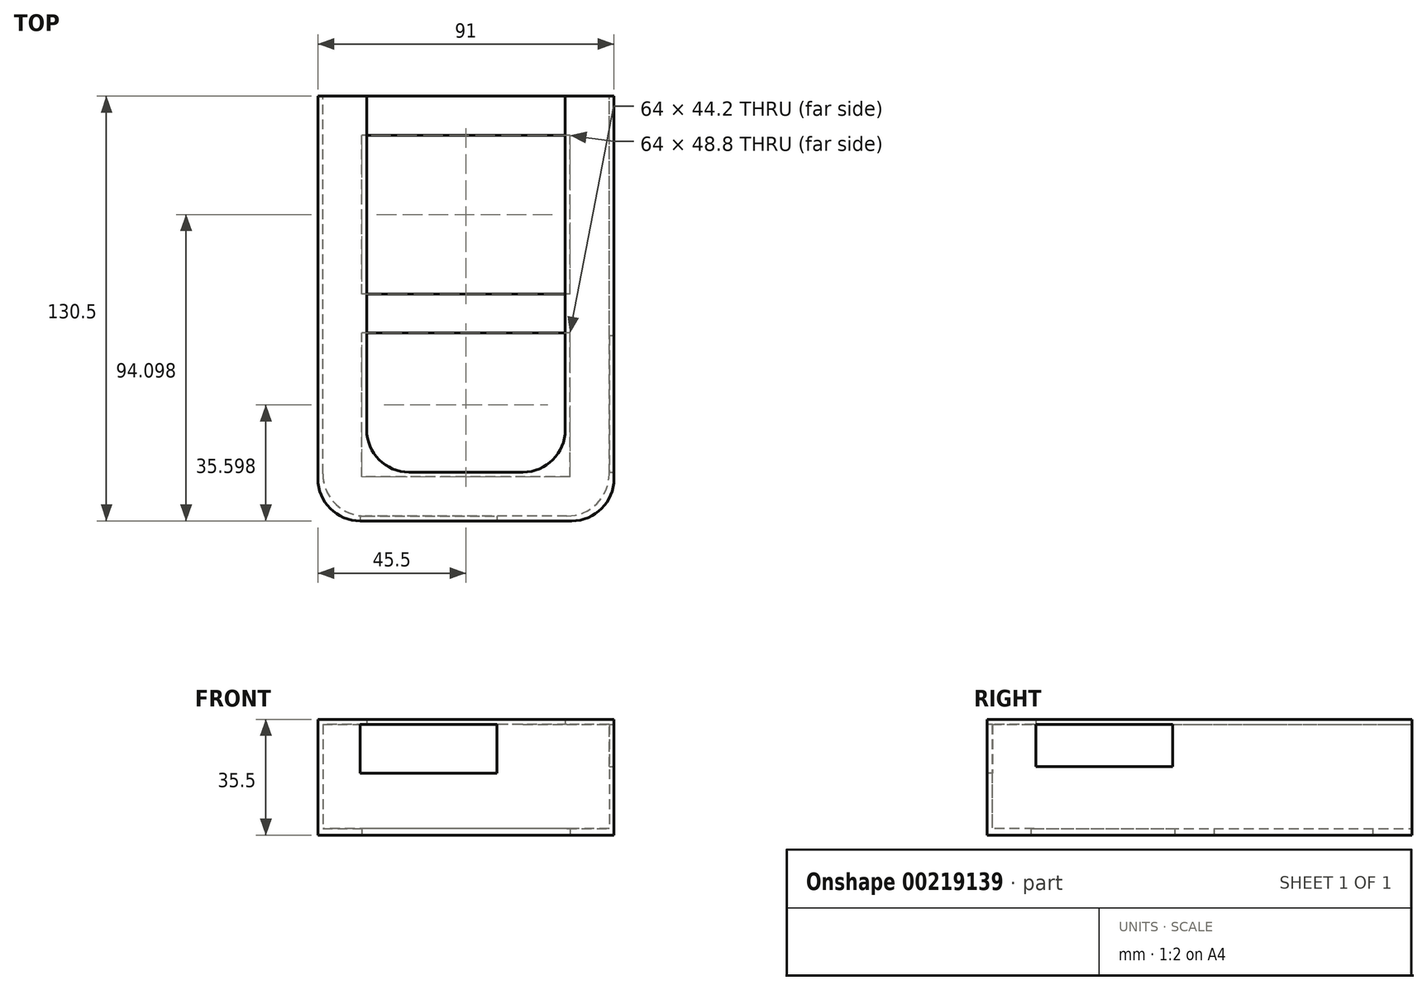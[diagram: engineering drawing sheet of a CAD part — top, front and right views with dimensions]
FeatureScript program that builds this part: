
annotation { "Feature Type Name" : "Feature", "Feature Type Description" : "" }
export const myFeature = defineFeature(function(context is Context, id is Id, definition is map)
    precondition{}
    {
        {
            var Q0;
            Q0=qCreatedBy(makeId("Top.planeOp"),FACE);
            var sketch = newSketch(context, id + "F0", { "sketchPlane" : qUnion([Q0])});
            skLineSegment(sketch, "E0.bottom", {"start": v(31, -64.5) * mm, "end": v(-31, -64.5) * mm});
            skLineSegment(sketch, "E0.top", {"start": v(44, 64.5) * mm, "end": v(-44, 64.5) * mm});
            skLineSegment(sketch, "E0.left", {"start": v(44, -51.5) * mm, "end": v(44, 64.5) * mm});
            skLineSegment(sketch, "E0.right", {"start": v(-44, -51.5) * mm, "end": v(-44, 64.5) * mm});
            skPoint(sketch, "E0.middle", {"position": v(0, 0) * mm});
            skLineSegment(sketch, "E1.bottom", {"start": v(32.5, -66) * mm, "end": v(-32.5, -66) * mm});
            skLineSegment(sketch, "E1.left", {"start": v(45.5, -53) * mm, "end": v(45.5, 64.5) * mm});
            skLineSegment(sketch, "E1.right", {"start": v(-45.5, -53) * mm, "end": v(-45.5, 64.5) * mm});
            skLineSegment(sketch, "E2", {"start": v(-44, 64.5) * mm, "end": v(-45.5, 64.5) * mm});
            skLineSegment(sketch, "E3", {"start": v(44, 64.5) * mm, "end": v(45.5, 64.5) * mm});
            skPoint(sketch, "E4.visualSharp", {"position": v(-44, -64.5) * mm});
            skArc(sketch, "E4.filletArc", {"start": v(-44, -51.5) * mm, "mid": v(-40.2, -60.7) * mm, "end": v(-31, -64.5) * mm});
            skPoint(sketch, "E5.visualSharp", {"position": v(-45.5, -66) * mm});
            skArc(sketch, "E5.filletArc", {"start": v(-45.5, -53) * mm, "mid": v(-41.7, -62.2) * mm, "end": v(-32.5, -66) * mm});
            skPoint(sketch, "E6.visualSharp", {"position": v(44, -64.5) * mm});
            skArc(sketch, "E6.filletArc", {"start": v(31, -64.5) * mm, "mid": v(40.2, -60.7) * mm, "end": v(44, -51.5) * mm});
            skPoint(sketch, "E7.visualSharp", {"position": v(45.5, -66) * mm});
            skArc(sketch, "E7.filletArc", {"start": v(32.5, -66) * mm, "mid": v(41.7, -62.2) * mm, "end": v(45.5, -53) * mm});
            skLineSegment(sketch, "E8.bottom", {"start": v(32, 3.7) * mm, "end": v(-32, 3.7) * mm});
            skLineSegment(sketch, "E8.top", {"start": v(32, 52.5) * mm, "end": v(-32, 52.5) * mm});
            skLineSegment(sketch, "E8.left", {"start": v(32, 3.7) * mm, "end": v(32, 52.5) * mm});
            skLineSegment(sketch, "E8.right", {"start": v(-32, 3.7) * mm, "end": v(-32, 52.5) * mm});
            skPoint(sketch, "E8.middle", {"position": v(0, 28.1) * mm});
            skLineSegment(sketch, "E9.bottom", {"start": v(32, -52.5) * mm, "end": v(-32, -52.5) * mm});
            skLineSegment(sketch, "E9.top", {"start": v(32, -8.3) * mm, "end": v(-32, -8.3) * mm});
            skLineSegment(sketch, "E9.left", {"start": v(32, -52.5) * mm, "end": v(32, -8.3) * mm});
            skLineSegment(sketch, "E9.right", {"start": v(-32, -52.5) * mm, "end": v(-32, -8.3) * mm});
            skPoint(sketch, "E9.middle", {"position": v(0, -30.4) * mm});
            skSolve(sketch);
        }
        {
            var Q0;
            Q0=makeQuery(id+"F0.imprint","IMPRINT",FACE,{"disambiguationData":[TD([[makeQuery(id+"F0.imprint","IMPRINT",EDGE,{"derivedFrom":sQuery(id+"F0.wireOp",EDGE,"E0.bottom")}),-1.0]])]});
            extrude(context, id + "F1", {"entities" : qUnion([Q0]), "depth" : 2 * mm});
        }
        {
            var Q0;
            Q0=makeQuery(id+"F0.imprint","IMPRINT",FACE,{"disambiguationData":[TD([[makeQuery(id+"F0.imprint","IMPRINT",EDGE,{"derivedFrom":sQuery(id+"F0.wireOp",EDGE,"E0.bottom")}),1.0]])]});
            extrude(context, id + "F2", {"entities" : qUnion([Q0]), "operationType" : NewBodyOperationType.ADD, "depth" : 34 * mm});
        }
        {
            var Q0;
            Q0=makeQuery(id+"F2.opExtrude","SWEPT_FACE",FACE,{"disambiguationData":[OSD([sQuery(id+"F0.wireOp",EDGE,"E1.left")])]});
            var sketch = newSketch(context, id + "F3", { "sketchPlane" : qUnion([Q0])});
            skPoint(sketch, "E10", {"position": v(-51, 34) * mm});
            skLineSegment(sketch, "E11.bottom", {"start": v(-51, 34) * mm, "end": v(-9, 34) * mm});
            skLineSegment(sketch, "E11.top", {"start": v(-51, 21) * mm, "end": v(-9, 21) * mm});
            skLineSegment(sketch, "E11.left", {"start": v(-51, 34) * mm, "end": v(-51, 21) * mm});
            skLineSegment(sketch, "E11.right", {"start": v(-9, 34) * mm, "end": v(-9, 21) * mm});
            skSolve(sketch);
        }
        {
            var Q0;
            Q0=makeQuery(id+"F3.imprint","IMPRINT",FACE,{"disambiguationData":[TD([[makeQuery(id+"F3.imprint","IMPRINT",EDGE,{"derivedFrom":sQuery(id+"F3.wireOp",EDGE,"E11.bottom")}),-1.0]])]});
            extrude(context, id + "F4", {"entities" : qUnion([Q0]), "operationType" : NewBodyOperationType.REMOVE, "oppositeDirection" : true, "depth" : 5 * mm});
        }
        {
            var Q0;
            Q0=makeQuery(id+"F2.opExtrude","SWEPT_FACE",FACE,{"disambiguationData":[OSD([sQuery(id+"F0.wireOp",EDGE,"E1.bottom")])]});
            var sketch = newSketch(context, id + "F5", { "sketchPlane" : qUnion([Q0])});
            skPoint(sketch, "E12", {"position": v(-35.5, 34) * mm});
            skLineSegment(sketch, "E13.bottom", {"start": v(-35.5, 34) * mm, "end": v(9.5, 34) * mm});
            skLineSegment(sketch, "E13.top", {"start": v(-35.5, 19) * mm, "end": v(9.5, 19) * mm});
            skLineSegment(sketch, "E13.left", {"start": v(-35.5, 34) * mm, "end": v(-35.5, 19) * mm});
            skLineSegment(sketch, "E13.right", {"start": v(9.5, 34) * mm, "end": v(9.5, 19) * mm});
            skSolve(sketch);
        }
        {
            var Q0;
            {var subQ4=sQuery(id+"F5.wireOp",EDGE,"E13.right");Q0=makeQuery(id+"F5.imprint","IMPRINT",FACE,{"disambiguationData":[TD([[makeQuery(id+"F5.imprint","IMPRINT",EDGE,{"derivedFrom":subQ4}),-1.0]])]});}
            extrude(context, id + "F6", {"entities" : qUnion([Q0]), "operationType" : NewBodyOperationType.REMOVE, "oppositeDirection" : true, "depth" : 5 * mm});
        }
        {
            var Q0;
            {var subQ0=sQuery(id+"F0.wireOp",EDGE,"E2");var subQ1=sQuery(id+"F0.wireOp",EDGE,"E0.left");var subQ2=sQuery(id+"F0.wireOp",EDGE,"E1.left");var subQ3=sQuery(id+"F0.wireOp",EDGE,"E3");Q0=makeQuery(id+"F4.boolean.opBoolean","SPLIT",FACE,{"disambiguationData":[TD([makeQuery(id+"F4.opExtrude","SWEPT_FACE",FACE,{"disambiguationData":[OSD([sQuery(id+"F3.wireOp",EDGE,"E11.right")])]})])],"derivedFrom":makeQuery(id+"F2.opExtrude","CAP_FACE",FACE,{"disambiguationData":[OSD([sQuery(id+"F0.wireOp",EDGE,"E0.bottom"),subQ1,sQuery(id+"F0.wireOp",EDGE,"E0.right"),sQuery(id+"F0.wireOp",EDGE,"E1.bottom"),subQ2,sQuery(id+"F0.wireOp",EDGE,"E1.right"),subQ0,subQ3,sQuery(id+"F0.wireOp",EDGE,"E4.filletArc"),sQuery(id+"F0.wireOp",EDGE,"E5.filletArc"),sQuery(id+"F0.wireOp",EDGE,"E6.filletArc"),sQuery(id+"F0.wireOp",EDGE,"E7.filletArc")])],"isStart":false})});}
            var sketch = newSketch(context, id + "F7", { "sketchPlane" : qUnion([Q0])});
            skLineSegment(sketch, "E14.bottom", {"start": v(45.5, 64.5) * mm, "end": v(30.5, 64.5) * mm});
            skLineSegment(sketch, "E14.top", {"start": v(32.5, -66) * mm, "end": v(-32.5, -66) * mm});
            skLineSegment(sketch, "E14.left", {"start": v(45.5, 64.5) * mm, "end": v(45.5, -53) * mm});
            skLineSegment(sketch, "E14.right", {"start": v(-45.5, 64.5) * mm, "end": v(-45.5, -53) * mm});
            skLineSegment(sketch, "E15.top", {"start": v(17.5, -51) * mm, "end": v(-17.5, -51) * mm});
            skLineSegment(sketch, "E15.left", {"start": v(30.5, 51) * mm, "end": v(30.5, -38) * mm});
            skLineSegment(sketch, "E15.right", {"start": v(-30.5, 51) * mm, "end": v(-30.5, -38) * mm});
            skPoint(sketch, "E15.middle", {"position": v(0, 0) * mm});
            skLineSegment(sketch, "E16", {"start": v(-30.5, 51) * mm, "end": v(-30.5, 64.5) * mm});
            skLineSegment(sketch, "E17", {"start": v(30.5, 51) * mm, "end": v(30.5, 64.5) * mm});
            skLineSegment(sketch, "E18.trimOffspring", {"start": v(-30.5, 64.5) * mm, "end": v(-45.5, 64.5) * mm});
            skPoint(sketch, "E19.visualSharp", {"position": v(-30.5, -51) * mm});
            skArc(sketch, "E19.filletArc", {"start": v(-30.5, -38) * mm, "mid": v(-26.7, -47.2) * mm, "end": v(-17.5, -51) * mm});
            skPoint(sketch, "E20.visualSharp", {"position": v(30.5, -51) * mm});
            skArc(sketch, "E20.filletArc", {"start": v(17.5, -51) * mm, "mid": v(26.7, -47.2) * mm, "end": v(30.5, -38) * mm});
            skPoint(sketch, "E21.visualSharp", {"position": v(45.5, -66) * mm});
            skArc(sketch, "E21.filletArc", {"start": v(32.5, -66) * mm, "mid": v(41.7, -62.2) * mm, "end": v(45.5, -53) * mm});
            skPoint(sketch, "E22.visualSharp", {"position": v(-45.5, -66) * mm});
            skArc(sketch, "E22.filletArc", {"start": v(-45.5, -53) * mm, "mid": v(-41.7, -62.2) * mm, "end": v(-32.5, -66) * mm});
            skSolve(sketch);
        }
        {
            var Q0;
            {var subQ9=sQuery(id+"F7.wireOp",EDGE,"E14.top");Q0=makeQuery(id+"F7.imprint","IMPRINT",FACE,{"disambiguationData":[TD([[makeQuery(id+"F7.imprint","IMPRINT",EDGE,{"derivedFrom":subQ9}),-1.0]])]});}
            var Q1;
            {var subQ2=sQuery(id+"F3.wireOp",EDGE,"E11.right");var subQ5=sQuery(id+"F0.wireOp",EDGE,"E1.left");var subQ9=makeQuery(id+"F4.boolean.opBoolean","COPY",EDGE,{"derivedFrom":makeQuery(id+"F4.opExtrude","SWEPT_EDGE",EDGE,{"disambiguationData":[OSD([subQ5,sQuery(id+"F3.wireOp",EDGE,"E11.bottom"),subQ2])]})});Q1=makeQuery(id+"F7.imprint","IMPRINT",FACE,{"disambiguationData":[TD([[makeQuery(id+"F7.imprint","IMPRINT",EDGE,{"derivedFrom":subQ9}),1.0]])]});}
            extrude(context, id + "F8", {"entities" : qUnion([Q0, Q1]), "operationType" : NewBodyOperationType.ADD, "depth" : 1.5 * mm});
        }
    });
